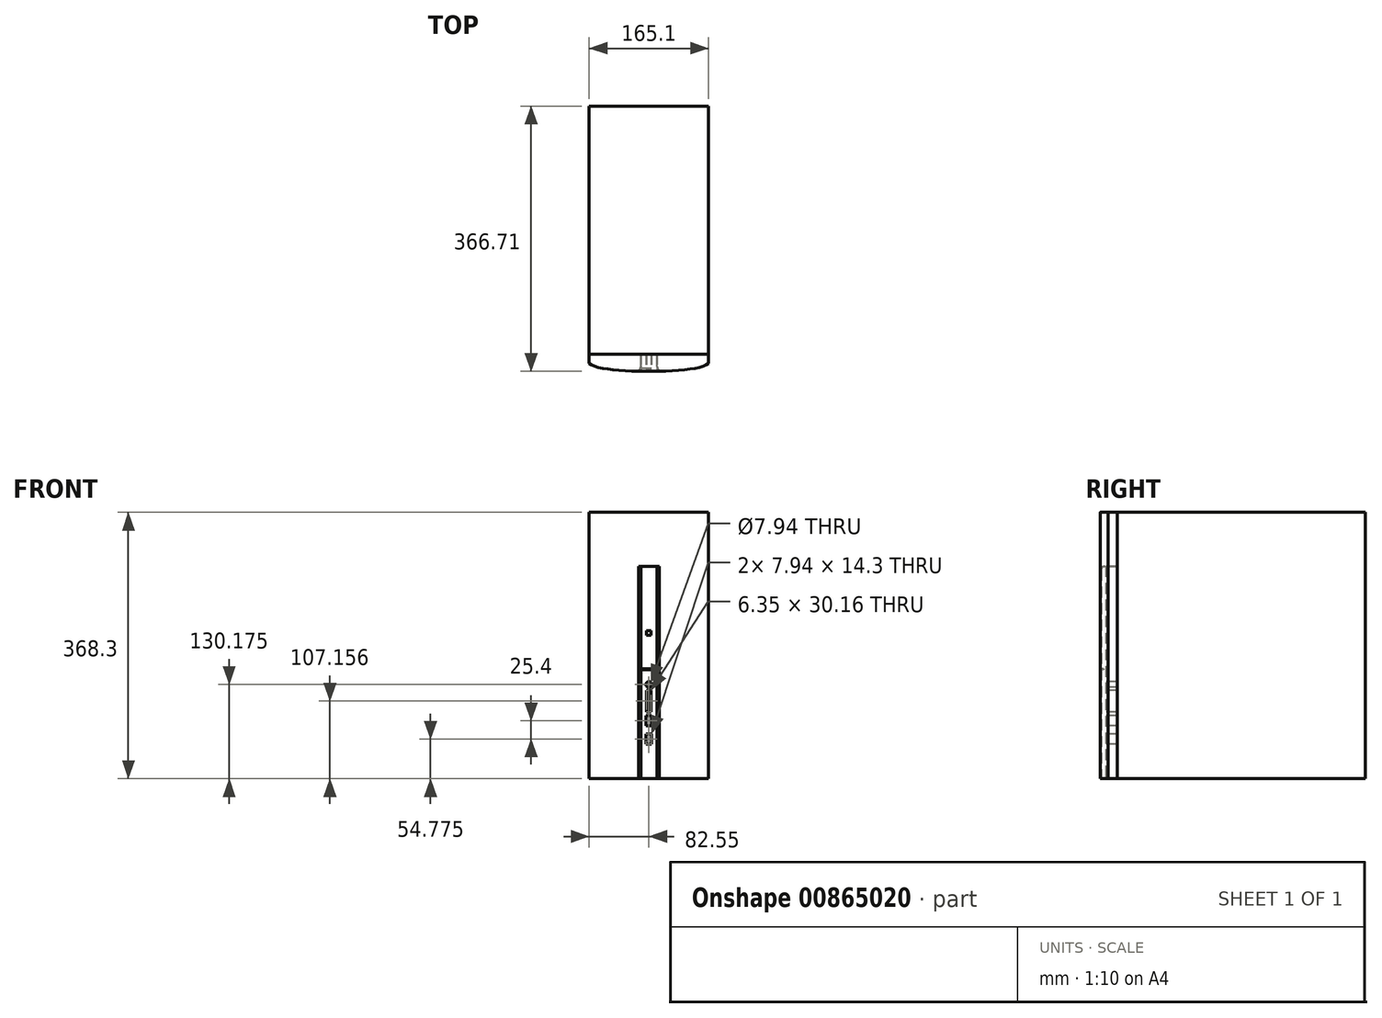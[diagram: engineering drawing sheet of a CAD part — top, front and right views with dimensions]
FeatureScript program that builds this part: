
annotation { "Feature Type Name" : "Feature", "Feature Type Description" : "" }
export const myFeature = defineFeature(function(context is Context, id is Id, definition is map)
    precondition{}
    {
        {
            var Q0;
            Q0=qCreatedBy(makeId("Top.planeOp"),FACE);
            var sketch = newSketch(context, id + "F0", { "sketchPlane" : qUnion([Q0])});
            skLineSegment(sketch, "E0.bottom", {"start": v(82.55, 171.45) * mm, "end": v(-82.55, 171.45) * mm});
            skLineSegment(sketch, "E0.top", {"start": v(82.55, -171.45) * mm, "end": v(-82.55, -171.45) * mm});
            skLineSegment(sketch, "E0.left", {"start": v(82.55, 171.45) * mm, "end": v(82.55, -171.45) * mm});
            skLineSegment(sketch, "E0.right", {"start": v(-82.55, 171.45) * mm, "end": v(-82.55, -171.45) * mm});
            skPoint(sketch, "E0.middle", {"position": v(0, 0) * mm});
            skSolve(sketch);
        }
        {
            var Q0;
            Q0=qSketchRegion(id+"F0",true);
            extrude(context, id + "F1", {"entities" : qUnion([Q0]), "depth" : 368.3 * mm, "offsetDistance" : 25.4 * mm});
        }
        {
            var Q0;
            Q0=qCreatedBy(makeId("Top.planeOp"),FACE);
            var sketch = newSketch(context, id + "F2", { "sketchPlane" : qUnion([Q0])});
            skLineSegment(sketch, "E1.bottom", {"start": v(-82.55, -171.45) * mm, "end": v(82.55, -171.45) * mm});
            skLineSegment(sketch, "E1.top", {"start": v(-82.55, -184.15) * mm, "end": v(82.55, -184.15) * mm});
            skLineSegment(sketch, "E1.left", {"start": v(-82.55, -171.45) * mm, "end": v(-82.55, -184.15) * mm});
            skLineSegment(sketch, "E1.right", {"start": v(82.55, -171.45) * mm, "end": v(82.55, -184.15) * mm});
            skFitSpline(sketch, "E2", {"points": [v(-82.55, -184.15) * mm, v(0, -195.26) * mm, v(82.55, -184.15) * mm], "startDerivative": vector(58, -53.1) * mm, "endDerivative": vector(58, 53.1) * mm});
            skSolve(sketch);
        }
        {
            var Q0;
            Q0=qSketchRegion(id+"F2",true);
            var Q1;
            Q1=makeQuery(id+"F1.opExtrude","CAP_FACE",FACE,{"disambiguationData":[OSD([sQuery(id+"F0.wireOp",EDGE,"E0.bottom"),sQuery(id+"F0.wireOp",EDGE,"E0.top"),sQuery(id+"F0.wireOp",EDGE,"E0.left"),sQuery(id+"F0.wireOp",EDGE,"E0.right")])],"isStart":false});
            extrude(context, id + "F3", {"entities" : qUnion([Q0]), "endBound" : BoundingType.UP_TO_SURFACE, "depth" : 368.3 * mm, "endBoundEntityFace" : qUnion([Q1]), "offsetDistance" : 25.4 * mm});
        }
        {
            var Q0;
            Q0=makeQuery(id+"F3.opExtrude","CAP_FACE",FACE,{"disambiguationData":[OSD([sQuery(id+"F2.wireOp",EDGE,"E1.bottom"),sQuery(id+"F2.wireOp",EDGE,"E1.left"),sQuery(id+"F2.wireOp",EDGE,"E1.right"),sQuery(id+"F2.wireOp",EDGE,"E2")])],"isStart":true});
            var sketch = newSketch(context, id + "F4", { "sketchPlane" : qUnion([Q0])});
            skLineSegment(sketch, "E3", {"start": v(-14.29, 195.14) * mm, "end": v(14.29, 195.14) * mm, "construction": true});
            skLineSegment(sketch, "E4.bottom", {"start": v(-11.11, 171.45) * mm, "end": v(11.11, 171.45) * mm});
            skLineSegment(sketch, "E4.top", {"start": v(-11.11, 187.33) * mm, "end": v(11.11, 187.33) * mm});
            skLineSegment(sketch, "E4.left", {"start": v(-11.11, 171.45) * mm, "end": v(-11.11, 187.33) * mm});
            skLineSegment(sketch, "E4.right", {"start": v(11.11, 171.45) * mm, "end": v(11.11, 187.33) * mm});
            skLineSegment(sketch, "E5", {"start": v(-11.11, 187.33) * mm, "end": v(-14.34, 195.26) * mm});
            skLineSegment(sketch, "E6", {"start": v(-14.34, 195.26) * mm, "end": v(14.34, 195.26) * mm});
            skLineSegment(sketch, "E7", {"start": v(14.34, 195.26) * mm, "end": v(11.11, 187.33) * mm});
            skSolve(sketch);
        }
        {
            var Q0;
            Q0=qSketchRegion(id+"F4",true);
            extrude(context, id + "F5", {"entities" : qUnion([Q0]), "operationType" : NewBodyOperationType.REMOVE, "oppositeDirection" : true, "depth" : 293.7 * mm, "offsetDistance" : 25.4 * mm});
        }
        {
            var Q0;
            {var subQ0=sQuery(id+"F2.wireOp",EDGE,"E2");var subQ1=sQuery(id+"F2.wireOp",EDGE,"E1.right");var subQ2=sQuery(id+"F2.wireOp",EDGE,"E1.bottom");Q0=makeQuery(id+"F5.boolean.opBoolean","SPLIT",FACE,{"disambiguationData":[TD([makeQuery(id+"F3.opExtrude","SWEPT_FACE",FACE,{"disambiguationData":[OSD([subQ1])]})])],"derivedFrom":makeQuery(id+"F3.opExtrude","CAP_FACE",FACE,{"disambiguationData":[OSD([subQ2,sQuery(id+"F2.wireOp",EDGE,"E1.left"),subQ1,subQ0])],"isStart":true})});}
            var sketch = newSketch(context, id + "F6", { "sketchPlane" : qUnion([Q0])});
            skLineSegment(sketch, "E8.bottom", {"start": v(-11.11, 171.45) * mm, "end": v(11.11, 171.45) * mm});
            skLineSegment(sketch, "E8.top", {"start": v(-11.11, 193.68) * mm, "end": v(11.11, 193.68) * mm});
            skLineSegment(sketch, "E8.left", {"start": v(-11.11, 171.45) * mm, "end": v(-11.11, 193.68) * mm});
            skLineSegment(sketch, "E8.right", {"start": v(11.11, 171.45) * mm, "end": v(11.11, 193.68) * mm});
            skPoint(sketch, "E9.visualSharp", {"position": v(-11.11, 193.68) * mm});
            skPoint(sketch, "E10.visualSharp", {"position": v(11.11, 193.68) * mm});
            skSolve(sketch);
        }
        {
            var Q0;
            {var subQ1=sQuery(id+"F6.wireOp",EDGE,"E8.bottom");Q0=makeQuery(id+"F6.imprint","IMPRINT",FACE,{"disambiguationData":[TD([[makeQuery(id+"F6.imprint","IMPRINT",EDGE,{"derivedFrom":subQ1}),1.0]])]});}
            var Q1;
            Q1=makeQuery(id+"F5.boolean.opBoolean","COPY",FACE,{"derivedFrom":makeQuery(id+"F5.opExtrude","CAP_FACE",FACE,{"disambiguationData":[OSD([sQuery(id+"F4.wireOp",EDGE,"E4.bottom"),sQuery(id+"F4.wireOp",EDGE,"E4.left"),sQuery(id+"F4.wireOp",EDGE,"E4.right"),sQuery(id+"F4.wireOp",EDGE,"E5"),sQuery(id+"F4.wireOp",EDGE,"E6"),sQuery(id+"F4.wireOp",EDGE,"E7")])],"isStart":false})});
            extrude(context, id + "F7", {"entities" : qUnion([Q0]), "endBound" : BoundingType.UP_TO_SURFACE, "oppositeDirection" : true, "depth" : 53.85 * mm, "endBoundEntityFace" : qUnion([Q1]), "offsetDistance" : 25.4 * mm});
        }
        {
            var Q0;
            Q0=makeQuery(id+"F7.opExtrude","CAP_EDGE",EDGE,{"disambiguationData":[OSD([sQuery(id+"F6.wireOp",EDGE,"E8.top")])],"isStart":false});
            fillet(context, id + "F8", {"entities" : qUnion([Q0]), "radius" : 5.08 * mm, "tangentPropagation" : true, "allowEdgeOverflow" : false});
        }
        {
            var Q0;
            Q0=makeQuery(id+"F7.opExtrude","SWEPT_FACE",FACE,{"disambiguationData":[OSD([sQuery(id+"F6.wireOp",EDGE,"E8.top")])]});
            var sketch = newSketch(context, id + "F9", { "sketchPlane" : qUnion([Q0])});
            skLineSegment(sketch, "E11.bottom", {"start": v(-11.11, 152) * mm, "end": v(11.11, 152) * mm});
            skLineSegment(sketch, "E11.top", {"start": v(-11.11, 150.81) * mm, "end": v(11.11, 150.81) * mm});
            skLineSegment(sketch, "E11.left", {"start": v(-11.11, 152) * mm, "end": v(-11.11, 150.81) * mm});
            skLineSegment(sketch, "E11.right", {"start": v(11.11, 152) * mm, "end": v(11.11, 150.81) * mm});
            skSolve(sketch);
        }
        {
            var Q0;
            Q0=qSketchRegion(id+"F9",true);
            extrude(context, id + "F10", {"entities" : qUnion([Q0]), "operationType" : NewBodyOperationType.REMOVE, "oppositeDirection" : true, "depth" : 3.17 * mm, "offsetDistance" : 25.4 * mm});
        }
        {
            var Q0;
            {var subQ0=sQuery(id+"F6.wireOp",EDGE,"E8.top");Q0=makeQuery(id+"F10.boolean.opBoolean","SPLIT",FACE,{"disambiguationData":[TD([makeQuery(id+"F8.opFillet","BLEND_FACE",FACE,{"disambiguationData":[OSD([subQ0])]})])],"derivedFrom":makeQuery(id+"F7.opExtrude","SWEPT_FACE",FACE,{"disambiguationData":[OSD([subQ0])]})});}
            var sketch = newSketch(context, id + "F11", { "sketchPlane" : qUnion([Q0])});
            skLineSegment(sketch, "E12.bottom", {"start": v(3.18, 198.04) * mm, "end": v(-3.17, 198.04) * mm});
            skLineSegment(sketch, "E12.top", {"start": v(3.18, 204.4) * mm, "end": v(-3.17, 204.4) * mm});
            skLineSegment(sketch, "E12.left", {"start": v(3.18, 198.04) * mm, "end": v(3.18, 204.4) * mm});
            skLineSegment(sketch, "E12.right", {"start": v(-3.17, 198.04) * mm, "end": v(-3.17, 204.4) * mm});
            skPoint(sketch, "E12.middle", {"position": v(0, 201.22) * mm});
            skPoint(sketch, "E12.middle.positionSnap0", {"position": v(0, 288.6) * mm});
            skPoint(sketch, "E12.centerSnap0", {"position": v(0, 288.6) * mm});
            skSolve(sketch);
        }
        {
            var Q0;
            Q0=makeQuery(id+"F11.imprint","IMPRINT",FACE,{"disambiguationData":[TD([[makeQuery(id+"F11.imprint","IMPRINT",EDGE,{"derivedFrom":sQuery(id+"F11.wireOp",EDGE,"E12.bottom")}),-1.0]])]});
            extrude(context, id + "F12", {"entities" : qUnion([Q0]), "operationType" : NewBodyOperationType.ADD, "depth" : 0.8 * mm, "offsetDistance" : 25.4 * mm});
        }
        {
            var Q0;
            {var subQ2=sQuery(id+"F6.wireOp",EDGE,"E8.top");Q0=makeQuery(id+"F10.boolean.opBoolean","SPLIT",FACE,{"disambiguationData":[TD([makeQuery(id+"F10.opExtrude","SWEPT_FACE",FACE,{"disambiguationData":[OSD([sQuery(id+"F9.wireOp",EDGE,"E11.top")])]})])],"derivedFrom":makeQuery(id+"F7.opExtrude","SWEPT_FACE",FACE,{"disambiguationData":[OSD([subQ2])]})});}
            var sketch = newSketch(context, id + "F13", { "sketchPlane" : qUnion([Q0])});
            skCircle(sketch, "E13", {"center": v(0, 130.18) * mm, "radius": 3.97 * mm});
            skLineSegment(sketch, "E14.bottom", {"start": v(3.17, 92.08) * mm, "end": v(-3.18, 92.08) * mm});
            skLineSegment(sketch, "E14.top", {"start": v(3.17, 122.24) * mm, "end": v(-3.18, 122.24) * mm});
            skLineSegment(sketch, "E14.left", {"start": v(3.17, 92.08) * mm, "end": v(3.17, 122.24) * mm});
            skLineSegment(sketch, "E14.right", {"start": v(-3.18, 92.08) * mm, "end": v(-3.18, 122.24) * mm});
            skPoint(sketch, "E14.middle", {"position": v(0, 107.16) * mm});
            skLineSegment(sketch, "E15.bottom", {"start": v(3.97, 73.03) * mm, "end": v(-3.97, 73.03) * mm});
            skLineSegment(sketch, "E15.top", {"start": v(3.97, 87.33) * mm, "end": v(-3.97, 87.33) * mm});
            skLineSegment(sketch, "E15.left", {"start": v(3.97, 73.03) * mm, "end": v(3.97, 87.33) * mm});
            skLineSegment(sketch, "E15.right", {"start": v(-3.97, 73.03) * mm, "end": v(-3.97, 87.33) * mm});
            skPoint(sketch, "E15.middle", {"position": v(0, 80.18) * mm});
            skLineSegment(sketch, "E16.bottom", {"start": v(3.97, 47.63) * mm, "end": v(-3.97, 47.63) * mm});
            skLineSegment(sketch, "E16.top", {"start": v(3.97, 61.93) * mm, "end": v(-3.97, 61.93) * mm});
            skLineSegment(sketch, "E16.left", {"start": v(3.97, 47.63) * mm, "end": v(3.97, 61.93) * mm});
            skLineSegment(sketch, "E16.right", {"start": v(-3.97, 47.62) * mm, "end": v(-3.97, 61.93) * mm});
            skPoint(sketch, "E16.middle", {"position": v(0, 54.78) * mm});
            skSolve(sketch);
        }
        {
            var Q0;
            Q0=qSketchRegion(id+"F13",true);
            var Q1;
            Q1=makeQuery(id+"F1.opExtrude","SWEPT_BODY",BODY,{"disambiguationData":[OSD([sQuery(id+"F0.wireOp",EDGE,"E0.bottom"),sQuery(id+"F0.wireOp",EDGE,"E0.top"),sQuery(id+"F0.wireOp",EDGE,"E0.left"),sQuery(id+"F0.wireOp",EDGE,"E0.right")])]});
            extrude(context, id + "F14", {"entities" : qUnion([Q0]), "operationType" : NewBodyOperationType.REMOVE, "endBound" : BoundingType.UP_TO_BODY, "oppositeDirection" : true, "depth" : 25.4 * mm, "endBoundEntityBody" : qUnion([Q1]), "offsetDistance" : 25.4 * mm});
        }
        {
            var Q0;
            Q0=qCreatedBy(makeId("Front.planeOp"),FACE);
            cPlane(context, id + "F15", {"entities" : qUnion([Q0]), "cplaneType" : CPlaneType.OFFSET, "offset" : 195.33 * mm, "width" : 152.4 * mm, "height" : 152.4 * mm});
        }
    });
